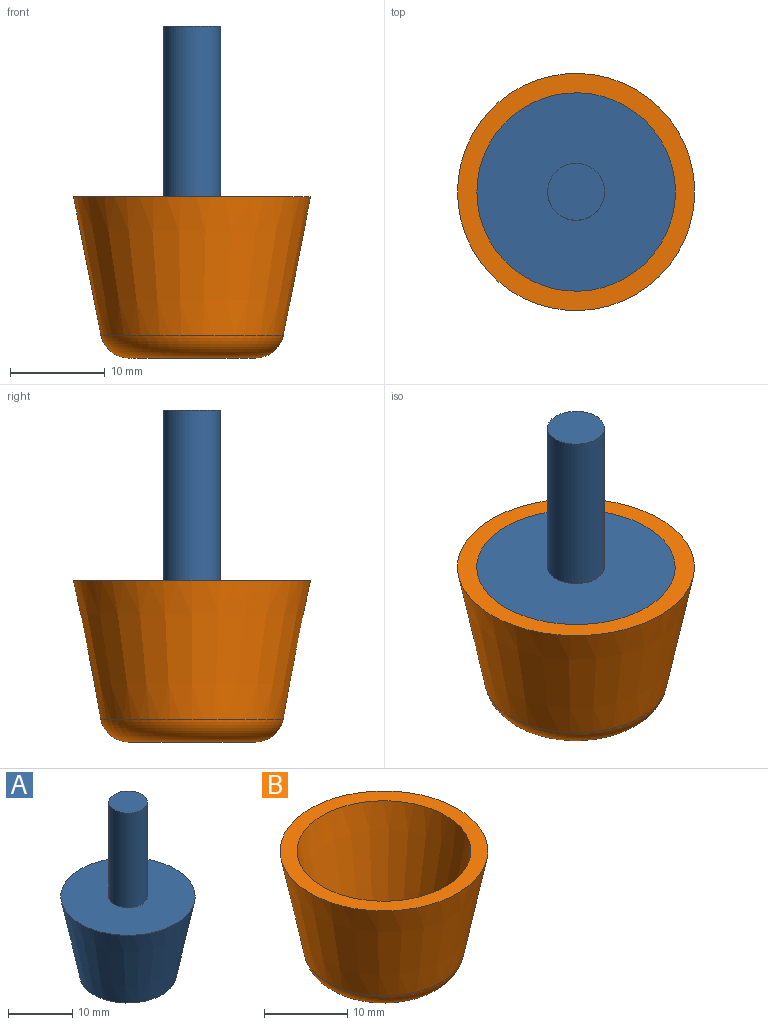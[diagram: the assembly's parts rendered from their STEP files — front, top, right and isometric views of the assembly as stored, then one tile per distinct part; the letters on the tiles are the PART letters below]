
ASSEMBLY  parts=2 mates=1
PART A: 5 faces, bbox 20.9x20.9x33 mm
  f0: plane 15x15mm, normal (0,0,-1), area 176.7mm2, adj f1
  f1: cone r=10.46mm half-angle=11.2deg, axis (0,0,1), area 862.7mm2, adj f0,f2
  f2: plane 20.92x20.92mm, normal (0,0,1), area 315.5mm2, adj f1,f3
  f3: cylinder r=3mm len=18mm, axis (0,0,-1), area 339.3mm2, adj f2,f4
  f4: plane 6x6mm, normal (0,0,1), area 28.3mm2, adj f3
PART B: 6 faces, bbox 25x25x17 mm
  f0: plane 25x25mm, normal (0,0,1), area 147.1mm2, adj f1,f4
  f1: cone r=10.46mm half-angle=11.2deg, axis (0,0,1), area 862.7mm2, adj f0,f2
  f2: plane 15x15mm, normal (0,0,1), area 176.7mm2, adj f1
  f3: plane 13.36x13.36mm, normal (0,0,-1), area 140.1mm2, adj f5
  f4: cone r=12.5mm half-angle=11.2deg, axis (0,0,1), area 1032.9mm2, adj f0,f5
  f5: torus R=6.68mm, axis (0,0,1), area 218.8mm2, adj f3,f4
PLACE A at identity fixed
PLACE B at identity
MATE fastened B.f1 <-> A.f1  axis (0,0,1) through (0,0,17)mm
